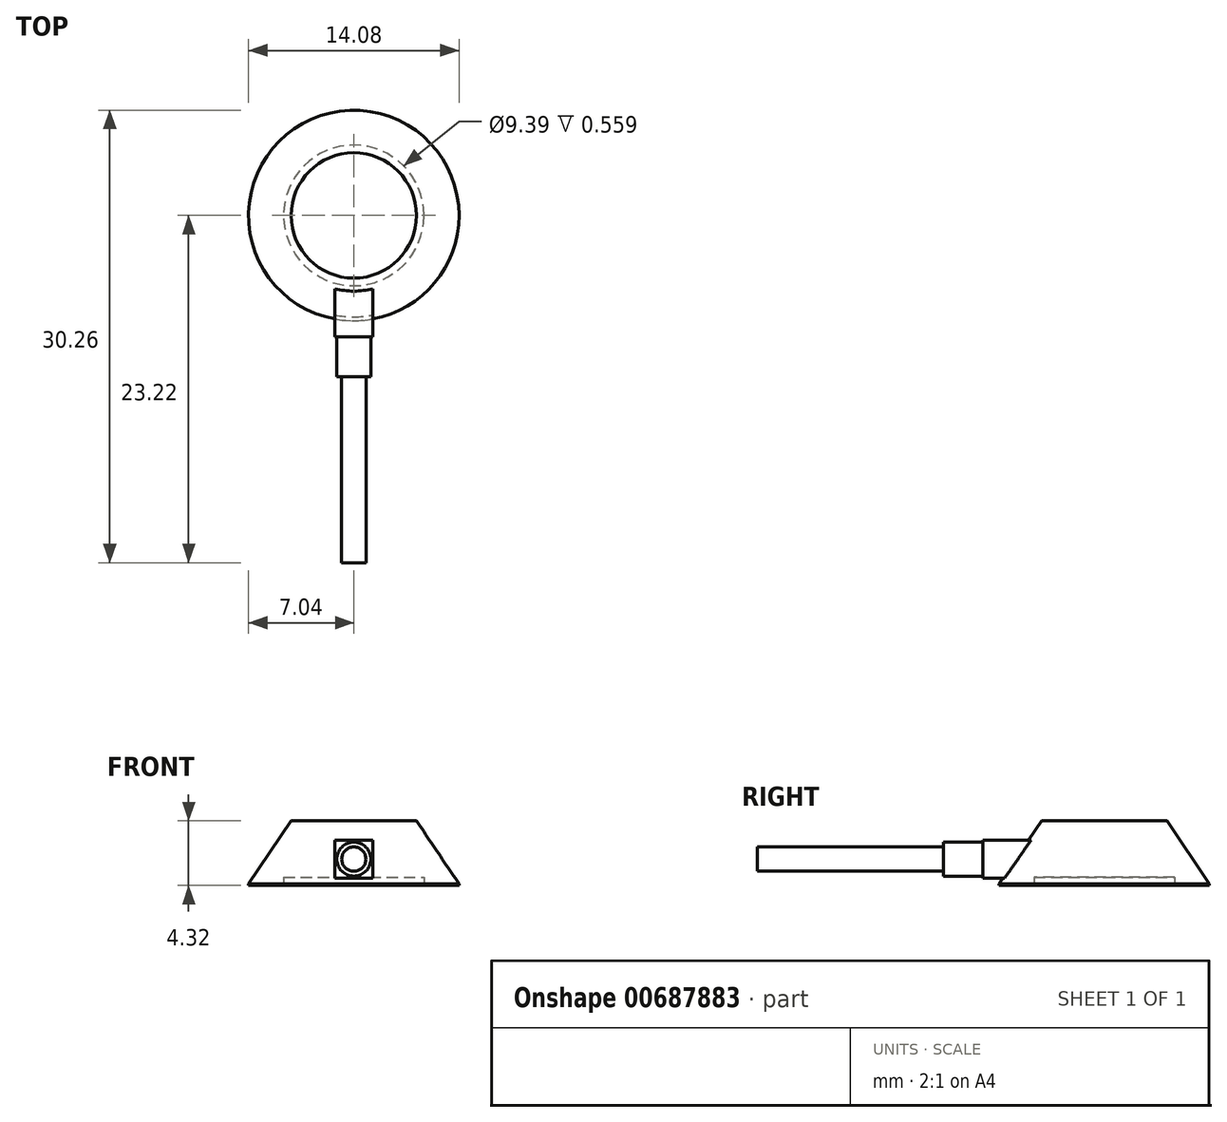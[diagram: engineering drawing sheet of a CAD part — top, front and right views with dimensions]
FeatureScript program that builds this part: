
annotation { "Feature Type Name" : "Feature", "Feature Type Description" : "" }
export const myFeature = defineFeature(function(context is Context, id is Id, definition is map)
    precondition{}
    {
        {
            var Q0;
            Q0=qCreatedBy(makeId("Top.planeOp"),FACE);
            var sketch = newSketch(context, id + "F0", { "sketchPlane" : qUnion([Q0])});
            skCircle(sketch, "E0", {"center": v(0, 0) * mm, "radius": 7.04 * mm});
            skSolve(sketch);
        }
        {
            var Q0;
            Q0 = qSketchRegion(id + "F0", true);
            extrude(context, id + "F1", {"entities" : qUnion([Q0]), "depth" : 4.32 * mm, "offsetDistance" : 25.4 * mm});
        }
        {
            var Q0;
            Q0=makeQuery(id+"F1.opExtrude","CAP_EDGE",EDGE,{"disambiguationData":[OSD([sQuery(id+"F0.wireOp",EDGE,"E0")])],"isStart":false});
            chamfer(context, id + "F2", {"entities" : qUnion([Q0]), "chamferType" : ChamferType.OFFSET_ANGLE, "width" : 2.84 * mm, "oppositeDirection" : false, "angle" : 56 * degree, "tangentPropagation" : true});
        }
        {
            var Q0;
            Q0=qCreatedBy(makeId("Front.planeOp"),FACE);
            var sketch = newSketch(context, id + "F3", { "sketchPlane" : qUnion([Q0])});
            skLineSegment(sketch, "E1.bottom", {"start": v(1.27, 0.48) * mm, "end": v(-1.27, 0.48) * mm});
            skLineSegment(sketch, "E1.top", {"start": v(1.27, 3.03) * mm, "end": v(-1.27, 3.03) * mm});
            skLineSegment(sketch, "E1.left", {"start": v(1.27, 0.48) * mm, "end": v(1.27, 3.03) * mm});
            skLineSegment(sketch, "E1.right", {"start": v(-1.27, 0.48) * mm, "end": v(-1.27, 3.03) * mm});
            skPoint(sketch, "E1.middle", {"position": v(0, 1.76) * mm});
            skSolve(sketch);
        }
        {
            var Q0;
            Q0 = qSketchRegion(id + "F3", true);
            extrude(context, id + "F4", {"entities" : qUnion([Q0]), "operationType" : NewBodyOperationType.ADD, "depth" : 8.13 * mm, "offsetDistance" : 25.4 * mm});
        }
        {
            var Q0;
            Q0=makeQuery(id+"F4.opExtrude","CAP_FACE",FACE,{"disambiguationData":[OSD([sQuery(id+"F3.wireOp",EDGE,"E1.bottom"),sQuery(id+"F3.wireOp",EDGE,"E1.top"),sQuery(id+"F3.wireOp",EDGE,"E1.left"),sQuery(id+"F3.wireOp",EDGE,"E1.right")])],"isStart":false});
            var sketch = newSketch(context, id + "F5", { "sketchPlane" : qUnion([Q0])});
            skCircle(sketch, "E2", {"center": v(0, 1.76) * mm, "radius": 1.14 * mm});
            skPoint(sketch, "E2.centerSnap0", {"position": v(-1.27, 1.76) * mm});
            skPoint(sketch, "E2.centerSnap1", {"position": v(0, 0.48) * mm});
            skSolve(sketch);
        }
        {
            var Q0;
            Q0 = qSketchRegion(id + "F5", true);
            extrude(context, id + "F6", {"entities" : qUnion([Q0]), "operationType" : NewBodyOperationType.ADD, "depth" : 2.64 * mm, "offsetDistance" : 25.4 * mm});
        }
        {
            var Q0;
            Q0=makeQuery(id+"F1.opExtrude","CAP_FACE",FACE,{"disambiguationData":[OSD([sQuery(id+"F0.wireOp",EDGE,"E0")])],"isStart":true});
            var sketch = newSketch(context, id + "F7", { "sketchPlane" : qUnion([Q0])});
            skCircle(sketch, "E3", {"center": v(0, 0) * mm, "radius": 4.7 * mm});
            skSolve(sketch);
        }
        {
            var Q0;
            Q0=makeQuery(id+"F7.imprint","IMPRINT",FACE,{"disambiguationData":[TD([[makeQuery(id+"F7.imprint","IMPRINT",EDGE,{"derivedFrom":sQuery(id+"F7.wireOp",EDGE,"E3")}),1.0]])]});
            extrude(context, id + "F8", {"entities" : qUnion([Q0]), "operationType" : NewBodyOperationType.REMOVE, "oppositeDirection" : true, "depth" : 0.56 * mm, "offsetDistance" : 25.4 * mm});
        }
        {
            var Q0;
            Q0=makeQuery(id+"F6.opExtrude","CAP_FACE",FACE,{"disambiguationData":[OSD([sQuery(id+"F5.wireOp",EDGE,"E2")])],"isStart":false});
            var sketch = newSketch(context, id + "F9", { "sketchPlane" : qUnion([Q0])});
            skCircle(sketch, "E4", {"center": v(0, 1.76) * mm, "radius": 0.81 * mm});
            skSolve(sketch);
        }
        {
            var Q0;
            Q0 = qSketchRegion(id + "F9", true);
            extrude(context, id + "F10", {"entities" : qUnion([Q0]), "operationType" : NewBodyOperationType.ADD, "depth" : 12.45 * mm, "offsetDistance" : 25.4 * mm});
        }
    });
